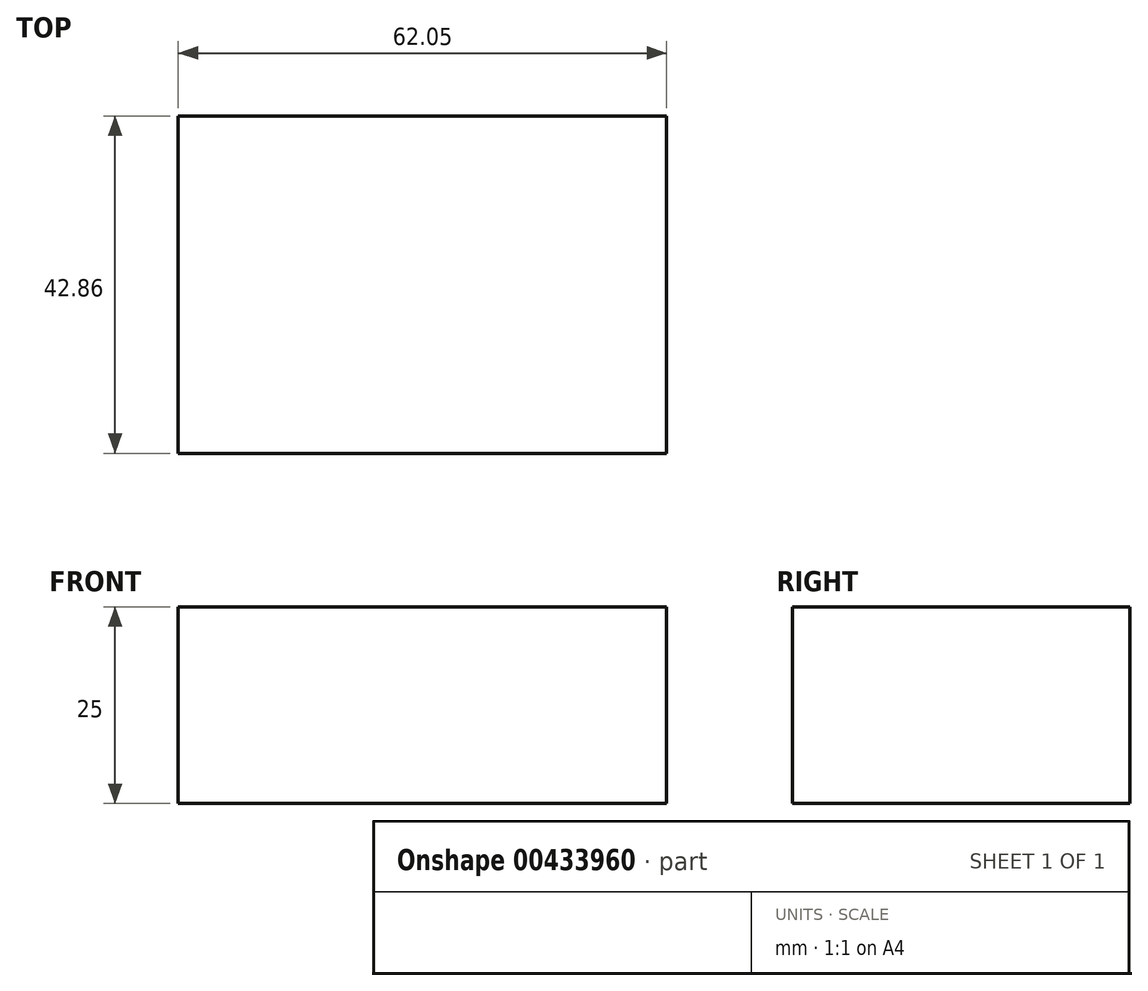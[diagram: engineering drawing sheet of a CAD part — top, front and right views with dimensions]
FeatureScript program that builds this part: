
annotation { "Feature Type Name" : "Feature", "Feature Type Description" : "" }
export const myFeature = defineFeature(function(context is Context, id is Id, definition is map)
    precondition{}
    {
        {
            var Q0;
            Q0=qCreatedBy(makeId("Top.planeOp"),FACE);
            var sketch = newSketch(context, id + "F0", { "sketchPlane" : qUnion([Q0])});
            skLineSegment(sketch, "E0.bottom", {"start": v(0, 0) * mm, "end": v(62.05, 0) * mm});
            skLineSegment(sketch, "E0.top", {"start": v(0, -42.86) * mm, "end": v(62.05, -42.86) * mm});
            skLineSegment(sketch, "E0.left", {"start": v(0, 0) * mm, "end": v(0, -42.86) * mm});
            skLineSegment(sketch, "E0.right", {"start": v(62.05, 0) * mm, "end": v(62.05, -42.86) * mm});
            skSolve(sketch);
        }
        {
            var Q0;
            Q0=makeQuery(id+"F0.imprint","IMPRINT",FACE,{"disambiguationData":[TD([[makeQuery(id+"F0.imprint","IMPRINT",EDGE,{"derivedFrom":sQuery(id+"F0.wireOp",EDGE,"E0.bottom")}),-1.0]])]});
            extrude(context, id + "F1", {"entities" : qUnion([Q0]), "depth" : 25 * mm});
        }
    });
